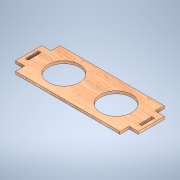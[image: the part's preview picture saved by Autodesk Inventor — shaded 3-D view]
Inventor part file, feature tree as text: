
AUTODESK INVENTOR PART (.ipt)
format: ipt  version: 2022 (Build 260153000, 153)  size: 165,888 bytes
history: native  units: mm
features: extrude x4, sketch x4, other x1
ambient origin geometry x8: Origin, YZ Plane, XZ Plane, XY Plane, X Axis, Y Axis, Z Axis, Center Point
bodies: Body1 (feature_tree)
feature tree (9):
  other  "Sólido1"
  extrude  "Extrusión1"  Depth=170.0mm
  extrude  "Extrusión2"  TaperAngle=0.0deg  [1 undecoded]
  extrude  "Extrusión3"  TaperAngle=180.0deg  [1 undecoded]
  extrude  "Extrusión4"  Depth=10.0mm TaperAngle=0.0deg
  sketch  "Boceto1"  dims[d0=400.0mm d1=170.0mm]
  sketch  "Boceto2"  dims[d2=10.0mm d3=0.0mm]
  sketch  "Boceto3"  dims[d5=100.0mm d6=180.0deg]
  sketch  "Boceto4"  dims[d7=120.0mm d8=10.0mm d9=0.0mm d10=70.0mm d11=100.0mm d12=10.0mm d13=0.0mm d14=17.5mm d15=0.0mm d16=10.0mm d17=50.0mm d18=10.0mm d19=0.0mm]
note: 2 required parameter values undecoded (feature->parameter linkage not recoverable at this tier; creation-order binding heuristic only, values carry confidence <= 0.55)
